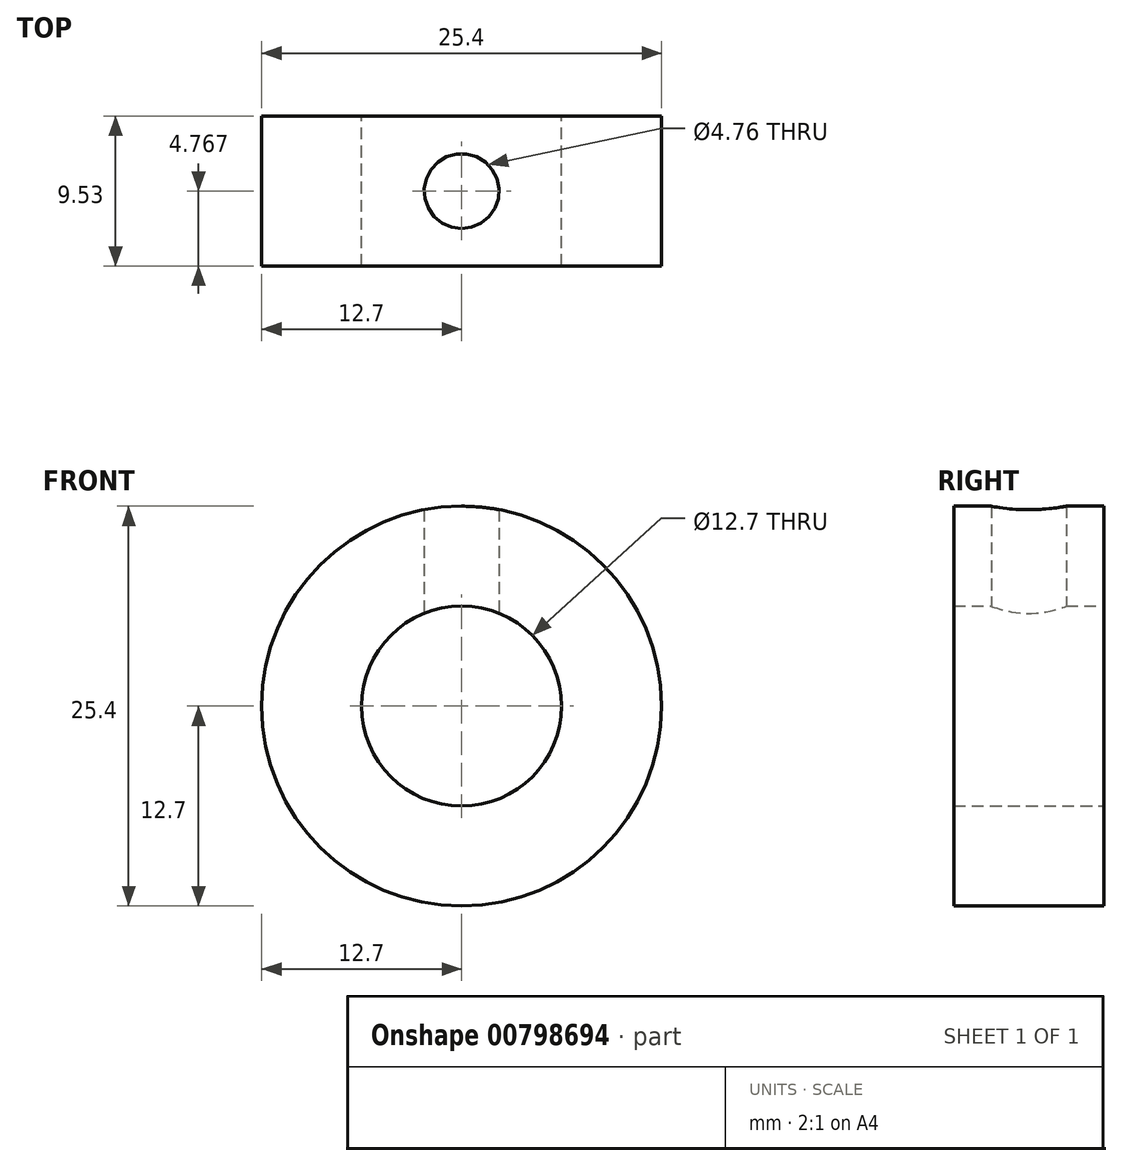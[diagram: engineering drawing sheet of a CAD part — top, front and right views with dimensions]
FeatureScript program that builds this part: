
annotation { "Feature Type Name" : "Feature", "Feature Type Description" : "" }
export const myFeature = defineFeature(function(context is Context, id is Id, definition is map)
    precondition{}
    {
        {
            var Q0;
            Q0=qCreatedBy(makeId("Front.planeOp"),FACE);
            var sketch = newSketch(context, id + "F0", { "sketchPlane" : qUnion([Q0])});
            skCircle(sketch, "E0", {"center": v(0, 0) * mm, "radius": 6.35 * mm});
            skCircle(sketch, "E1.0", {"center": v(0, 0) * mm, "radius": 12.7 * mm});
            skSolve(sketch);
        }
        {
            var Q0;
            Q0=makeQuery(id+"F0.imprint","IMPRINT",FACE,{"disambiguationData":[TD([[makeQuery(id+"F0.imprint","IMPRINT",EDGE,{"derivedFrom":sQuery(id+"F0.wireOp",EDGE,"E0")}),-1.0]])]});
            extrude(context, id + "F1", {"entities" : qUnion([Q0]), "depth" : 9.52 * mm, "offsetDistance" : 25.4 * mm});
        }
        {
            var Q0;
            Q0=qCreatedBy(makeId("Top.planeOp"),FACE);
            var sketch = newSketch(context, id + "F2", { "sketchPlane" : qUnion([Q0])});
            skCircle(sketch, "E2", {"center": v(0, -4.76) * mm, "radius": 2.38 * mm});
            skSolve(sketch);
        }
        {
            var Q0;
            Q0 = qSketchRegion(id + "F2", true);
            extrude(context, id + "F3", {"entities" : qUnion([Q0]), "operationType" : NewBodyOperationType.REMOVE, "depth" : 25.4 * mm, "offsetDistance" : 25.4 * mm});
        }
    });
